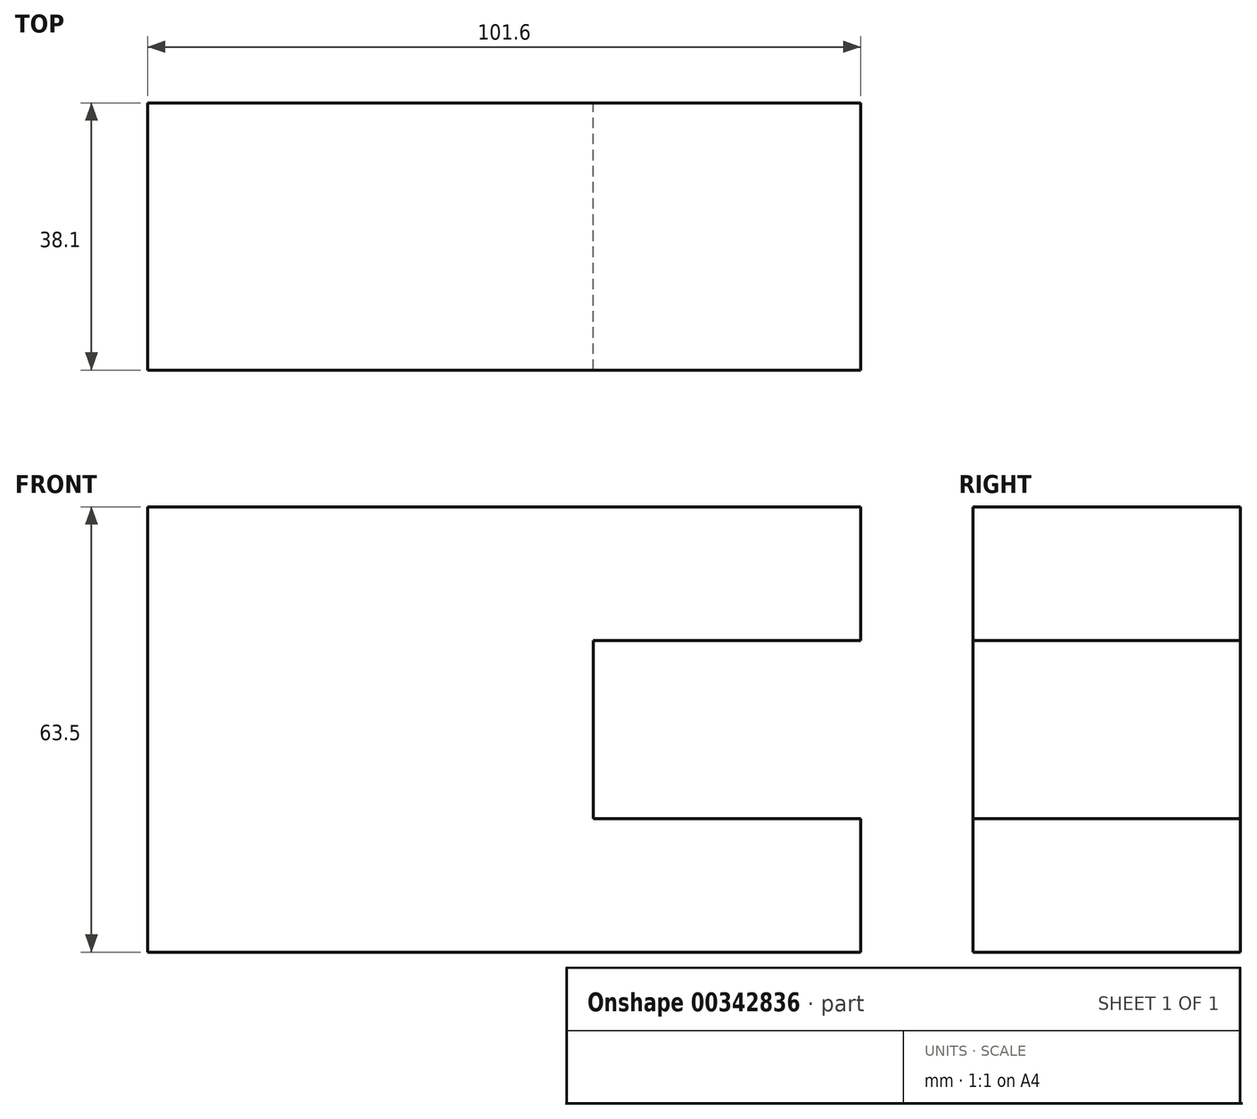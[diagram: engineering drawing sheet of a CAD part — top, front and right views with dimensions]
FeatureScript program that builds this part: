
annotation { "Feature Type Name" : "Feature", "Feature Type Description" : "" }
export const myFeature = defineFeature(function(context is Context, id is Id, definition is map)
    precondition{}
    {
        {
            var Q0;
            Q0=qCreatedBy(makeId("Front.planeOp"),FACE);
            var sketch = newSketch(context, id + "F0", { "sketchPlane" : qUnion([Q0])});
            skLineSegment(sketch, "E0", {"start": v(-37.02, 56.07) * mm, "end": v(-37.02, -7.43) * mm});
            skLineSegment(sketch, "E1", {"start": v(-37.02, 56.07) * mm, "end": v(64.58, 56.07) * mm});
            skLineSegment(sketch, "E2", {"start": v(64.58, 56.07) * mm, "end": v(64.58, 37.02) * mm});
            skLineSegment(sketch, "E3", {"start": v(64.58, 37.02) * mm, "end": v(26.48, 37.02) * mm});
            skLineSegment(sketch, "E4", {"start": v(26.48, 37.02) * mm, "end": v(26.48, 11.62) * mm});
            skLineSegment(sketch, "E5", {"start": v(26.48, 11.62) * mm, "end": v(64.58, 11.62) * mm});
            skLineSegment(sketch, "E6", {"start": v(64.58, 11.62) * mm, "end": v(64.58, -7.43) * mm});
            skLineSegment(sketch, "E7", {"start": v(64.58, -7.43) * mm, "end": v(-37.02, -7.43) * mm});
            skSolve(sketch);
        }
        {
            var Q0;
            Q0=makeQuery(id+"F0.imprint","IMPRINT",FACE,{"disambiguationData":[TD([[makeQuery(id+"F0.imprint","IMPRINT",EDGE,{"derivedFrom":sQuery(id+"F0.wireOp",EDGE,"E0")}),1.0]])]});
            extrude(context, id + "F1", {"entities" : qUnion([Q0]), "depth" : 38.1 * mm});
        }
    });
